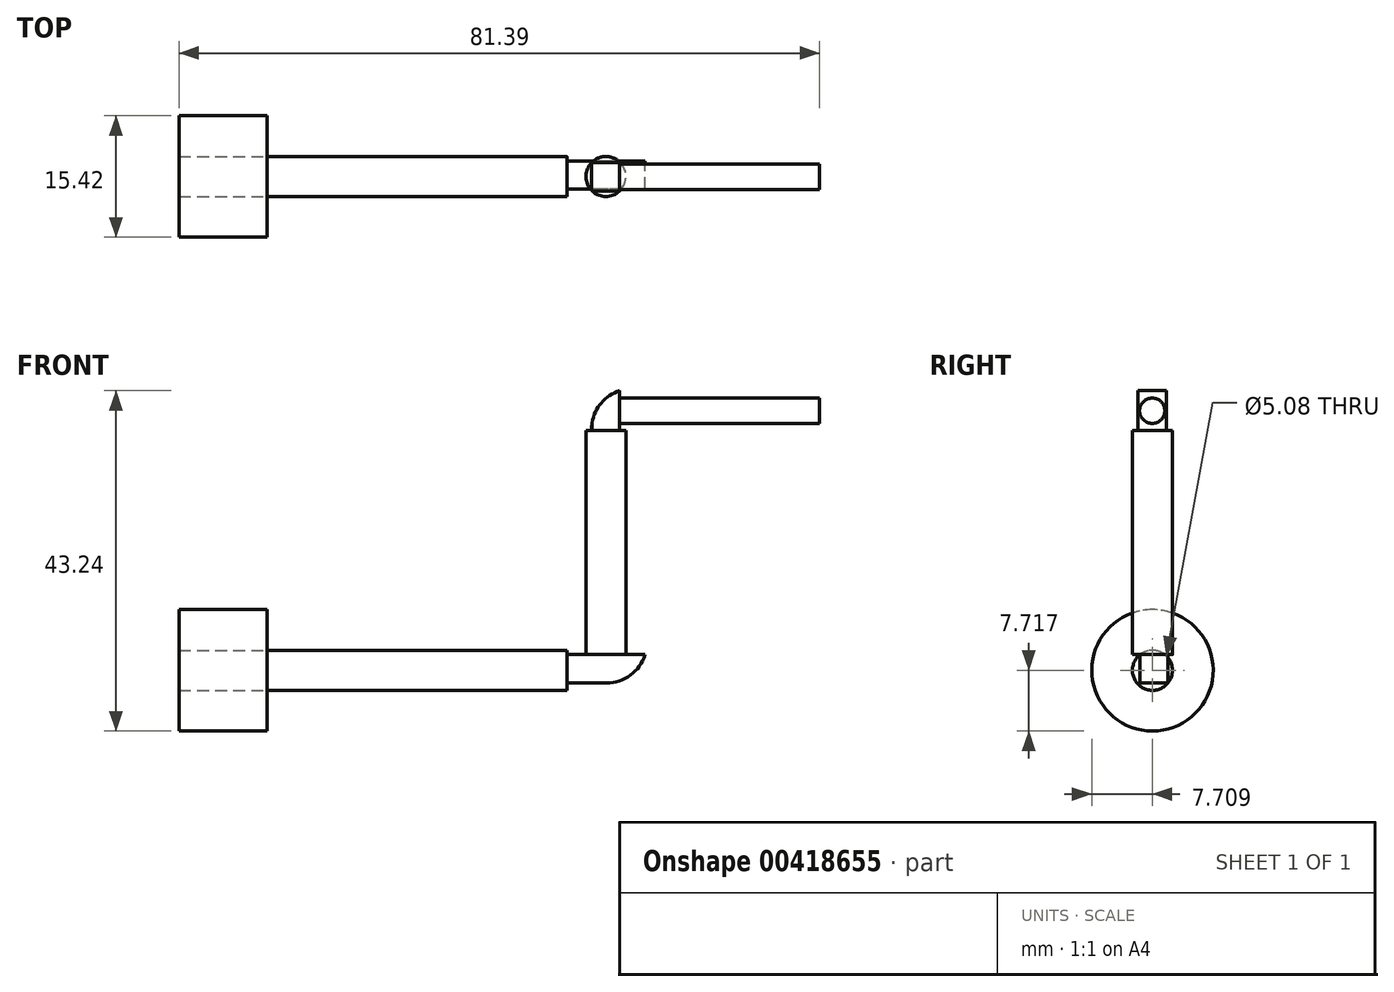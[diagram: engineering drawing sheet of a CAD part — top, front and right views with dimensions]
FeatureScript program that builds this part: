
annotation { "Feature Type Name" : "Feature", "Feature Type Description" : "" }
export const myFeature = defineFeature(function(context is Context, id is Id, definition is map)
    precondition{}
    {
        {
            var Q0;
            Q0=qCreatedBy(makeId("Right.planeOp"),FACE);
            var sketch = newSketch(context, id + "F0", { "sketchPlane" : qUnion([Q0])});
            skCircle(sketch, "E0", {"center": v(-112.04, 54.15) * mm, "radius": 2.54 * mm});
            skCircle(sketch, "E1", {"center": v(-112.04, 54.15) * mm, "radius": 7.71 * mm});
            skSolve(sketch);
        }
        {
            var Q0;
            Q0=makeQuery(id+"F0.imprint","IMPRINT",FACE,{"disambiguationData":[TD([[makeQuery(id+"F0.imprint","IMPRINT",EDGE,{"derivedFrom":sQuery(id+"F0.wireOp",EDGE,"E0")}),1.0]])]});
            extrude(context, id + "F1", {"entities" : qUnion([Q0]), "depth" : 38.1 * mm, "offsetDistance" : 25.4 * mm});
        }
        {
            var Q0;
            Q0=makeQuery(id+"F1.opExtrude","CAP_FACE",FACE,{"disambiguationData":[OSD([sQuery(id+"F0.wireOp",EDGE,"E0")])],"isStart":false});
            var sketch = newSketch(context, id + "F2", { "sketchPlane" : qUnion([Q0])});
            skLineSegment(sketch, "E2.bottom", {"start": v(-113.62, 56.14) * mm, "end": v(-110.08, 56.14) * mm});
            skLineSegment(sketch, "E2.top", {"start": v(-113.62, 52.54) * mm, "end": v(-110.08, 52.54) * mm});
            skLineSegment(sketch, "E2.left", {"start": v(-113.62, 56.14) * mm, "end": v(-113.62, 52.54) * mm});
            skLineSegment(sketch, "E2.right", {"start": v(-110.08, 56.14) * mm, "end": v(-110.08, 52.54) * mm});
            skSolve(sketch);
        }
        {
            var Q0;
            Q0 = qSketchRegion(id + "F2", true);
            extrude(context, id + "F3", {"entities" : qUnion([Q0]), "operationType" : NewBodyOperationType.ADD, "depth" : 9.9 * mm});
        }
        {
            var Q0;
            Q0=makeQuery(id+"F3.opExtrude","CAP_EDGE",EDGE,{"disambiguationData":[OSD([sQuery(id+"F2.wireOp",EDGE,"E2.top")])],"isStart":false});
            fillet(context, id + "F4", {"entities" : qUnion([Q0]), "radius" : 5.08 * mm, "tangentPropagation" : true, "allowEdgeOverflow" : false});
        }
        {
            var Q0;
            Q0=makeQuery(id+"F3.opExtrude","SWEPT_FACE",FACE,{"disambiguationData":[OSD([sQuery(id+"F2.wireOp",EDGE,"E2.bottom")])]});
            var sketch = newSketch(context, id + "F5", { "sketchPlane" : qUnion([Q0])});
            skCircle(sketch, "E3", {"center": v(43.05, -112.04) * mm, "radius": 2.54 * mm});
            skPoint(sketch, "E3.centerSnap0", {"position": v(38.1, -112.04) * mm});
            skPoint(sketch, "E3.centerSnap1", {"position": v(43.05, -113.62) * mm});
            skSolve(sketch);
        }
        {
            var Q0;
            Q0 = qSketchRegion(id + "F5", true);
            extrude(context, id + "F6", {"entities" : qUnion([Q0]), "operationType" : NewBodyOperationType.ADD, "depth" : 28.45 * mm, "offsetDistance" : 25.4 * mm});
        }
        {
            var Q0;
            Q0=makeQuery(id+"F0.imprint","IMPRINT",FACE,{"disambiguationData":[TD([[makeQuery(id+"F0.imprint","IMPRINT",EDGE,{"derivedFrom":sQuery(id+"F0.wireOp",EDGE,"E0")}),-1.0]])]});
            extrude(context, id + "F7", {"entities" : qUnion([Q0]), "oppositeDirection" : true, "depth" : 11.18 * mm, "offsetDistance" : 25.4 * mm});
        }
        {
            var Q0;
            Q0=makeQuery(id+"F6.opExtrude","CAP_FACE",FACE,{"disambiguationData":[OSD([sQuery(id+"F5.wireOp",EDGE,"E3")])],"isStart":false});
            var sketch = newSketch(context, id + "F8", { "sketchPlane" : qUnion([Q0])});
            skLineSegment(sketch, "E4.left", {"start": v(40.52, -112.2) * mm, "end": v(40.52, -112.22) * mm});
            skLineSegment(sketch, "E4.right", {"start": v(45.59, -112.2) * mm, "end": v(45.59, -112.22) * mm});
            skLineSegment(sketch, "E5.bottom", {"start": v(41.24, -110.26) * mm, "end": v(44.8, -110.26) * mm});
            skLineSegment(sketch, "E5.top", {"start": v(41.24, -113.88) * mm, "end": v(44.8, -113.88) * mm});
            skLineSegment(sketch, "E5.left", {"start": v(41.24, -110.26) * mm, "end": v(41.24, -113.88) * mm});
            skLineSegment(sketch, "E5.right", {"start": v(44.8, -110.26) * mm, "end": v(44.8, -113.88) * mm});
            skSolve(sketch);
        }
        {
            var Q0;
            {var subQ1=sQuery(id+"F8.wireOp",EDGE,"E5.bottom");Q0=makeQuery(id+"F8.imprint","IMPRINT",FACE,{"disambiguationData":[TD([[makeQuery(id+"F8.imprint","IMPRINT",EDGE,{"derivedFrom":subQ1}),-1.0]])]});}
            extrude(context, id + "F9", {"entities" : qUnion([Q0]), "operationType" : NewBodyOperationType.ADD, "depth" : 5.08 * mm, "offsetDistance" : 25.4 * mm});
        }
        {
            var Q0;
            Q0=makeQuery(id+"F9.opExtrude","CAP_EDGE",EDGE,{"disambiguationData":[OSD([sQuery(id+"F8.wireOp",EDGE,"E5.left")])],"isStart":false});
            fillet(context, id + "F10", {"entities" : qUnion([Q0]), "radius" : 5.08 * mm, "tangentPropagation" : true, "allowEdgeOverflow" : false});
        }
        {
            var Q0;
            Q0=makeQuery(id+"F9.opExtrude","SWEPT_FACE",FACE,{"disambiguationData":[OSD([sQuery(id+"F8.wireOp",EDGE,"E5.right")])]});
            var sketch = newSketch(context, id + "F11", { "sketchPlane" : qUnion([Q0])});
            skCircle(sketch, "E6", {"center": v(-112.07, 87.13) * mm, "radius": 1.6 * mm});
            skPoint(sketch, "E6.centerSnap0", {"position": v(-110.26, 87.13) * mm});
            skPoint(sketch, "E6.centerSnap1", {"position": v(-112.07, 84.59) * mm});
            skSolve(sketch);
        }
        {
            var Q0;
            Q0 = qSketchRegion(id + "F11", true);
            extrude(context, id + "F12", {"entities" : qUnion([Q0]), "operationType" : NewBodyOperationType.ADD, "depth" : 25.4 * mm, "offsetDistance" : 25.4 * mm});
        }
    });
